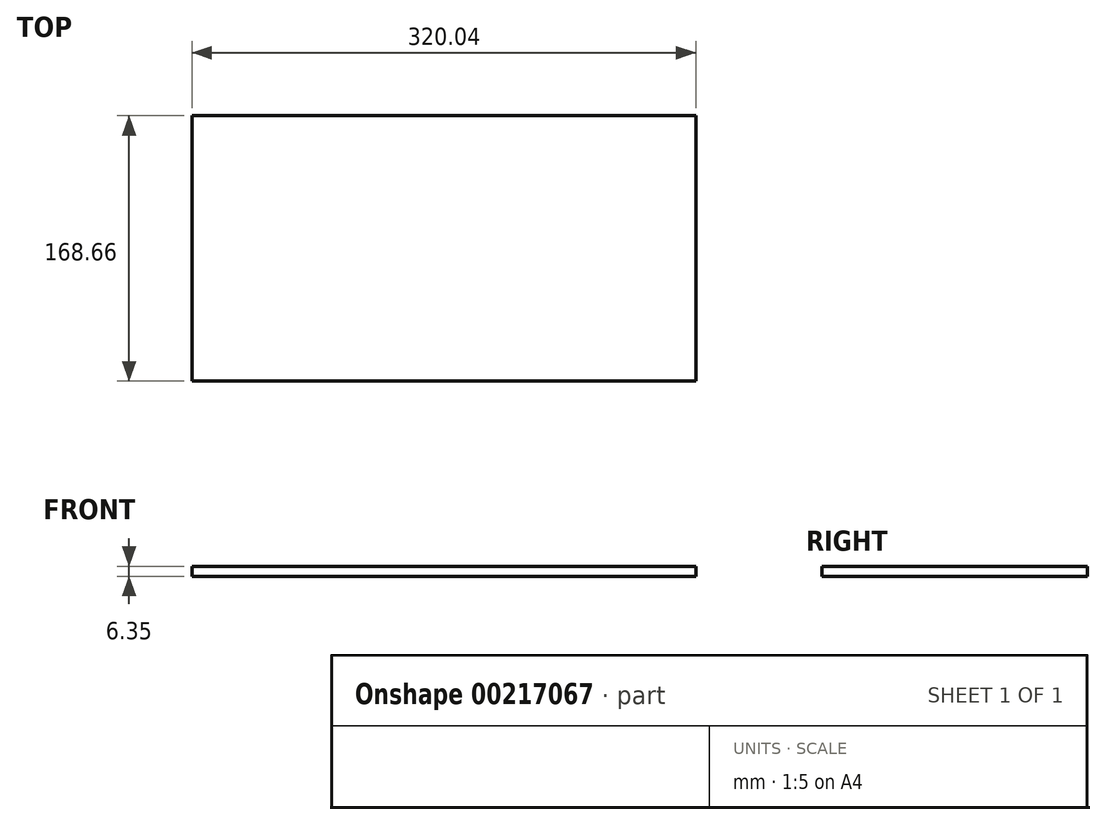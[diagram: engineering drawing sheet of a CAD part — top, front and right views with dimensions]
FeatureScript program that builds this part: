
annotation { "Feature Type Name" : "Feature", "Feature Type Description" : "" }
export const myFeature = defineFeature(function(context is Context, id is Id, definition is map)
    precondition{}
    {
        {
            var Q0;
            Q0=qCreatedBy(makeId("Top.planeOp"),FACE);
            var sketch = newSketch(context, id + "F0", { "sketchPlane" : qUnion([Q0])});
            skLineSegment(sketch, "E0.bottom", {"start": v(160.02, -84.33) * mm, "end": v(-160.02, -84.33) * mm});
            skLineSegment(sketch, "E0.top", {"start": v(160.02, 84.33) * mm, "end": v(-160.02, 84.33) * mm});
            skLineSegment(sketch, "E0.left", {"start": v(160.02, -84.33) * mm, "end": v(160.02, 84.33) * mm});
            skLineSegment(sketch, "E0.right", {"start": v(-160.02, -84.33) * mm, "end": v(-160.02, 84.33) * mm});
            skPoint(sketch, "E0.middle", {"position": v(0, 0) * mm});
            skSolve(sketch);
        }
        {
            var Q0;
            Q0 = qSketchRegion(id + "F0", true);
            extrude(context, id + "F1", {"entities" : qUnion([Q0]), "depth" : 6.35 * mm});
        }
    });
